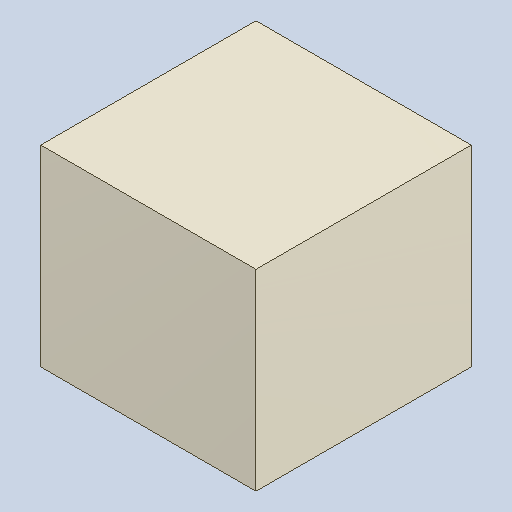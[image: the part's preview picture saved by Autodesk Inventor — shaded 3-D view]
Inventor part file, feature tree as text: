
AUTODESK INVENTOR PART (.ipt)
format: ipt  version: 2023.4 (Build 274418000, 418)  size: 81,920 bytes
history: native  units: mm
features: extrude x1
ambient origin geometry x8: Origin, YZ Plane, XZ Plane, XY Plane, X Axis, Y Axis, Z Axis, Center Point
bodies: Solid1 (feature_tree)
feature tree (1):
  extrude  "Extruded_4"  [1 undecoded]
note: 1 required parameter value undecoded (feature->parameter linkage not recoverable at this tier; creation-order binding heuristic only, values carry confidence <= 0.55)
